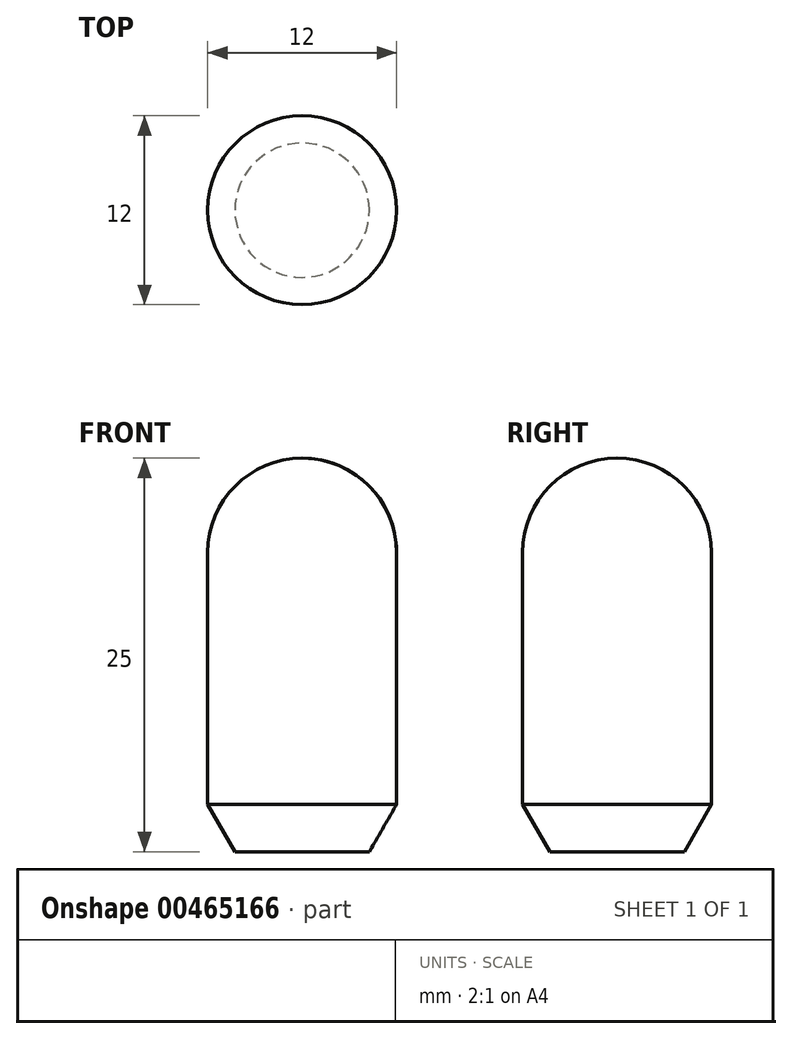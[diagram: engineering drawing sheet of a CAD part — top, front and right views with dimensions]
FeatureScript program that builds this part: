
annotation { "Feature Type Name" : "Feature", "Feature Type Description" : "" }
export const myFeature = defineFeature(function(context is Context, id is Id, definition is map)
    precondition{}
    {
        {
            var Q0;
            Q0=qCreatedBy(makeId("Top.planeOp"),FACE);
            var sketch = newSketch(context, id + "F0", { "sketchPlane" : qUnion([Q0])});
            skCircle(sketch, "E0", {"center": v(0, 0) * mm, "radius": 6 * mm});
            skSolve(sketch);
        }
        {
            var Q0;
            Q0=qSketchRegion(id+"F0",true);
            extrude(context, id + "F1", {"entities" : qUnion([Q0]), "depth" : 25 * mm});
        }
        {
            var Q0;
            Q0=makeQuery(id+"F1.opExtrude","CAP_EDGE",EDGE,{"disambiguationData":[OSD([sQuery(id+"F0.wireOp",EDGE,"E0")])],"isStart":false});
            fillet(context, id + "F2", {"entities" : qUnion([Q0]), "radius" : 6 * mm, "tangentPropagation" : true, "allowEdgeOverflow" : false});
        }
        {
            var Q0;
            Q0=makeQuery(id+"F1.opExtrude","CAP_EDGE",EDGE,{"disambiguationData":[OSD([sQuery(id+"F0.wireOp",EDGE,"E0")])],"isStart":true});
            chamfer(context, id + "F3", {"entities" : qUnion([Q0]), "chamferType" : ChamferType.OFFSET_ANGLE, "width" : 3 * mm, "oppositeDirection" : false, "angle" : 30 * degree, "tangentPropagation" : true});
        }
    });
